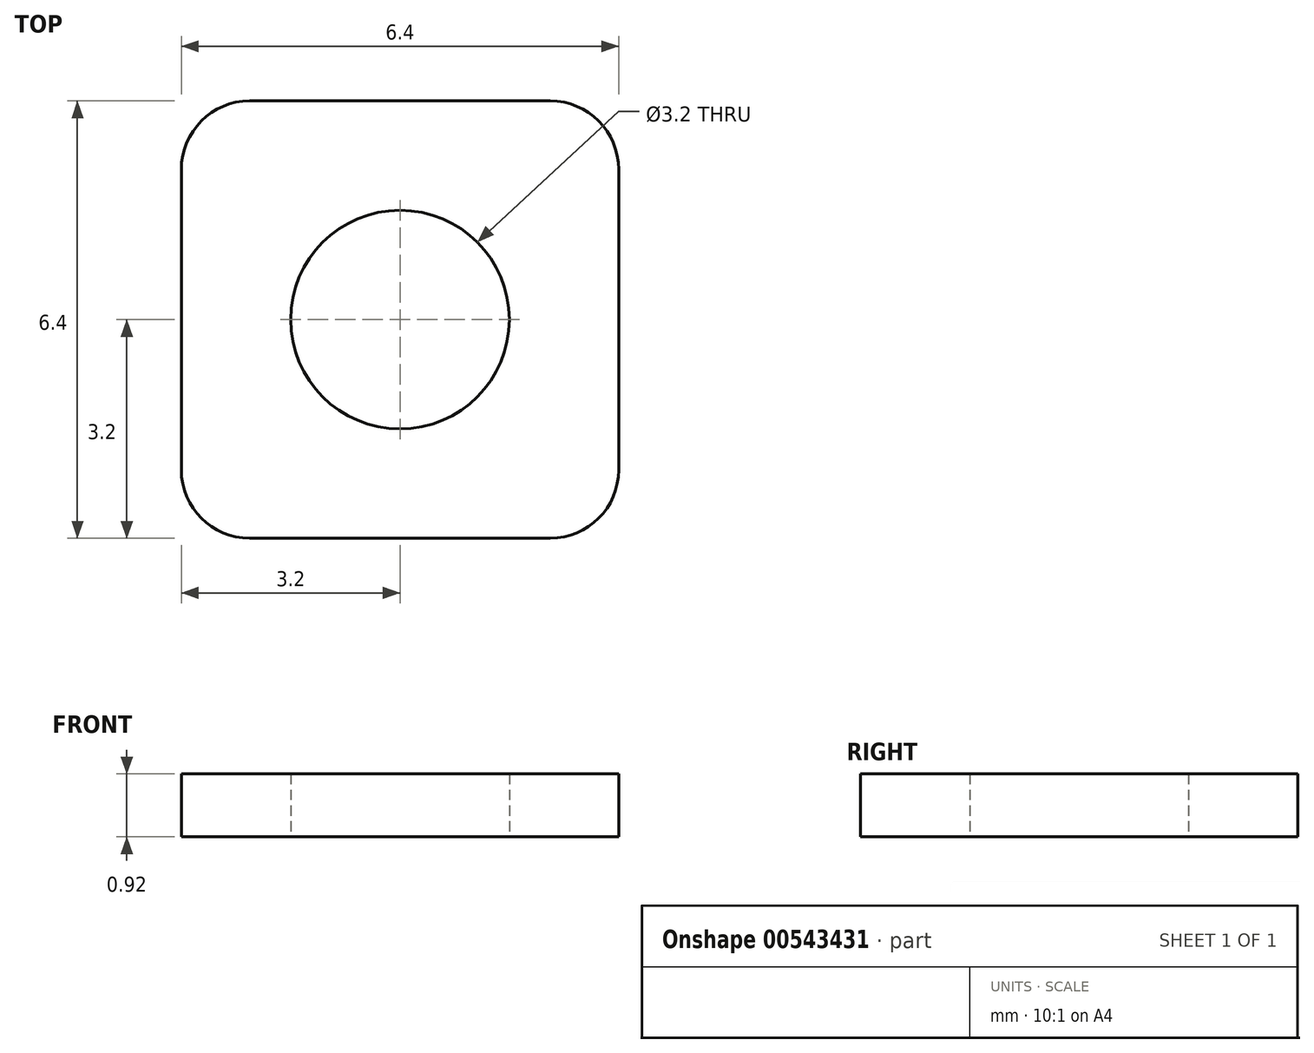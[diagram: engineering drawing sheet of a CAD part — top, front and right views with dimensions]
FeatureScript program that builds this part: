
annotation { "Feature Type Name" : "Feature", "Feature Type Description" : "" }
export const myFeature = defineFeature(function(context is Context, id is Id, definition is map)
    precondition{}
    {
        {
            var Q0;
            Q0=qCreatedBy(makeId("Top.planeOp"),FACE);
            var sketch = newSketch(context, id + "F0", { "sketchPlane" : qUnion([Q0])});
            skLineSegment(sketch, "E0.bottom", {"start": v(2.2, -3.2) * mm, "end": v(-2.2, -3.2) * mm});
            skLineSegment(sketch, "E0.top", {"start": v(2.2, 3.2) * mm, "end": v(-2.2, 3.2) * mm});
            skLineSegment(sketch, "E0.left", {"start": v(3.2, -2.2) * mm, "end": v(3.2, 2.2) * mm});
            skLineSegment(sketch, "E0.right", {"start": v(-3.2, -2.2) * mm, "end": v(-3.2, 2.2) * mm});
            skPoint(sketch, "E0.middle", {"position": v(0, 0) * mm});
            skPoint(sketch, "E1.visualSharp", {"position": v(-3.2, 3.2) * mm});
            skArc(sketch, "E1.filletArc", {"start": v(-2.2, 3.2) * mm, "mid": v(-2.9, 2.9) * mm, "end": v(-3.2, 2.2) * mm});
            skPoint(sketch, "E2.visualSharp", {"position": v(3.2, 3.2) * mm});
            skArc(sketch, "E2.filletArc", {"start": v(3.2, 2.2) * mm, "mid": v(2.9, 2.9) * mm, "end": v(2.2, 3.2) * mm});
            skPoint(sketch, "E3.visualSharp", {"position": v(-3.2, -3.2) * mm});
            skArc(sketch, "E3.filletArc", {"start": v(-3.2, -2.2) * mm, "mid": v(-2.9, -2.9) * mm, "end": v(-2.2, -3.2) * mm});
            skPoint(sketch, "E4.visualSharp", {"position": v(3.2, -3.2) * mm});
            skArc(sketch, "E4.filletArc", {"start": v(2.2, -3.2) * mm, "mid": v(2.9, -2.9) * mm, "end": v(3.2, -2.2) * mm});
            skCircle(sketch, "E5", {"center": v(0, 0) * mm, "radius": 1.6 * mm});
            skSolve(sketch);
        }
        {
            var Q0;
            Q0=makeQuery(id+"F0.imprint","IMPRINT",FACE,{"disambiguationData":[TD([[makeQuery(id+"F0.imprint","IMPRINT",EDGE,{"derivedFrom":sQuery(id+"F0.wireOp",EDGE,"E0.bottom")}),-1.0]])]});
            extrude(context, id + "F1", {"entities" : qUnion([Q0]), "depth" : 0.92 * mm, "offsetDistance" : 25 * mm});
        }
    });
